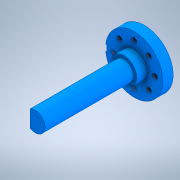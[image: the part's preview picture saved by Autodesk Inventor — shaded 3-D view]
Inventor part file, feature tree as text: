
AUTODESK INVENTOR PART (.ipt)
format: ipt  version: 2021 (Build 250183000, 183)  size: 180,224 bytes
history: native  units: mm
features: sketch x7, extrude x6, plane x2, other x1, hole x1, pattern_circular x1
ambient origin geometry x8: Origin, YZ Plane, XZ Plane, XY Plane, X Axis, Y Axis, Z Axis, Center Point
bodies: Body1 (feature_tree)
feature tree (18):
  other  "Sólido1"
  extrude  "Extrusión1"  Depth=4.0mm TaperAngle=0.0deg
  hole  "Agujero1"  [1 undecoded]
  pattern_circular  "Patrón circular1"  Count=8 Angle=360.0deg
  extrude  "Extrusión2"  Depth=2.9mm TaperAngle=0.0deg
  extrude  "Extrusión3"  Depth=5.0mm TaperAngle=0.0deg
  extrude  "Extrusión4"  Depth=4.0mm TaperAngle=0.0deg
  extrude  "Extrusión5"  Depth=34.0mm TaperAngle=0.0deg
  plane  "Plano de trabajo1"
  plane  "Plano de trabajo2"
  extrude  "Extrusión7"  Depth=2.5mm
  sketch  "Boceto1"  dims[d0=22.0mm d1=4.0mm d2=0.0mm]
  sketch  "Boceto2"  dims[d3=8.0mm d4=2.0mm]
  sketch  "Boceto3"  dims[d5=2.013mm d6=5.0mm d7=4.0mm d8=2.0mm d9=90.0deg d10=8.0mm d11=20.594885mm d12=80.0mm d13=360.0deg]
  sketch  "Boceto4"  dims[d15=8.8mm d16=2.9mm d17=0.0mm]
  sketch  "Boceto5"  dims[d18=5.0mm d19=2.6mm d20=0.0mm]
  sketch  "Boceto6"  dims[d21=10.0mm d22=4.0mm d23=0.0mm]
  sketch  "Boceto8"  dims[d26=1.9mm d27=34.0mm d28=0.0mm d33=2.5mm d34=4.0mm d35=0.5mm d36=0.0mm d37=0.5mm d38=0.872665mm d39=0.5mm d40=0.872665mm]
note: 1 required parameter value undecoded (feature->parameter linkage not recoverable at this tier; creation-order binding heuristic only, values carry confidence <= 0.55)
